# Revit family: Plum Fix_Shower_Argent_Architectura Start Classic Rail Set
name_source: partatom
category: Plumbing Fixtures
revit_build: Autodesk Revit 2016 (Build: 20190508_0715(x64)
units: mm (PartAtom-declared; Revit-internal decimal feet)

## family parameters
Always vertical = Yes
Cut with Voids When Loaded = No
OmniClass Number = 23.45.05.14.14
OmniClass Title = Sinks/Lavatories
Part Type = Normal
Room Calculation Point = No
Round Connector Dimension = Use Diameter
Shared = No
Work Plane-Based = No

## types (1)
- Chrome (VSR04061B)
    Body Material = z_Argent_Chrome
    CW Connection = No
    Cost = 0 $
    Description = Architectura Start Classic 110-600 Rail set
    HW Connection = No
    IfcExportAs = IfcSanitaryTerminal
    IfcExportType = SHOWER
    Manufacturer = Argent
    Manufacturer_Overall Depth = 76 mm
    Manufacturer_Overall Height = 600 mm
    Manufacturer_Overall Width = 110 mm
    Manufacturer_Spec Code = VSR04061B
    Manufacturer_URL__Product Specific = https://www.argentaust.com.au
    Model = VSR04061B
    ModifiedIssue_ANZRS = 20200421 $
    Soap Dish Material = z_Argent_Clear Plastic
    Type Comments = 3 Tap Hole
    URL = https://www.argentaust.com.au
    Uniclass2015Code = Pr_40_20_87_75
    Uniclass2015Title = Shower fittings package
    Uniclass2015Version = Products v1.17
    Vent Connection = No
    Waste Connection = No

## geometry (parser evidence)
native form markers: Sweep x2
no freeform markers — native parametric forms only
